# Revit family: BOX BV GRAN
name_source: partatom
category: Modelos genéricos
revit_build: Autodesk Revit 2017 (Build: 20160225_1515(x64)
units: mm (PartAtom-declared; Revit-internal decimal feet)

## family parameters
Compartido = No
Corte con vacíos al cargar = No
Cota de conector redondo = Diámetro de uso
Puede alojar armadura = No
Punto de cálculo de habitación = No
Se basa en plano de trabajo = No
Siempre vertical = Sí
Tipo de pieza = Normal

## types (4) — shared parameters
AmplePeu = 60 mm  [stored 0.19685 ft]
EspBoca = 3 mm  [stored 0.00984252 ft]
EspPeu = 3 mm  [stored 0.00984252 ft]
Fabricante = Casals Ventilación
K = 100 mm  [stored 0.328084 ft]
Material = <Por categoría>
S = 17 mm
URL = www.casals.com

## per-type parameters (varying)
| type | A | AlturaBoca | AmpleBoca | B | C | Dext | Dimensiones | F | G | I | M | O | VisiblePeuMig | Z | eEXT |
| BOX BV 20/20 | 1101 mm | 1017 mm  [stored 3.33661 ft] | 1001 mm | 1117 mm  [stored 3.6647 ft] | 1525 mm  [stored 5.00328 ft] | 605 mm  [stored 1.98491 ft] | 1100,5x1117x1541,8 | 85 mm  [stored 0.278871 ft] | 425 mm  [stored 1.39436 ft] | 1298 mm  [stored 4.25853 ft] | 1412 mm | 484 mm | No | 57 mm | 607 mm |
| BOX BV 22/22 | 1351 mm | 1100 mm | 1251 mm | 1200 mm | 1683 mm | 658 mm  [stored 2.15879 ft] | 1350,5x1200x1699,8 | 85 mm  [stored 0.278871 ft] | 422 mm | 1548 mm  [stored 5.07874 ft] | 1570 mm | 484 mm | No | 57 mm | 694 mm |
| BOX BV 25/25 | 1458 mm | 1238 mm | 1358 mm | 1338 mm | 1810 mm | 768 mm  [stored 2.51969 ft] | 1457,5x1337,5x1826,8 | 98 mm  [stored 0.321522 ft] | 444 mm | 1655 mm | 1697 mm | 526 mm | Sí | 57 mm | 796 mm  [stored 2.61155 ft] |
| BOX BV 30/28 | 1651 mm | 1472 mm  [stored 4.8294 ft] | 1551 mm | 1572 mm | 2040 mm | 893 mm  [stored 2.92979 ft] | 1650,5x1572x1056,8 | 100 mm  [stored 0.328084 ft] | 536 mm | 1848 mm | 1912 mm | 595 mm  [stored 1.9521 ft] | Sí | 64 mm | 937 mm |

note: [stored X ft] marks values corroborated as IEEE doubles in the binary element streams (Revit-internal decimal feet)
